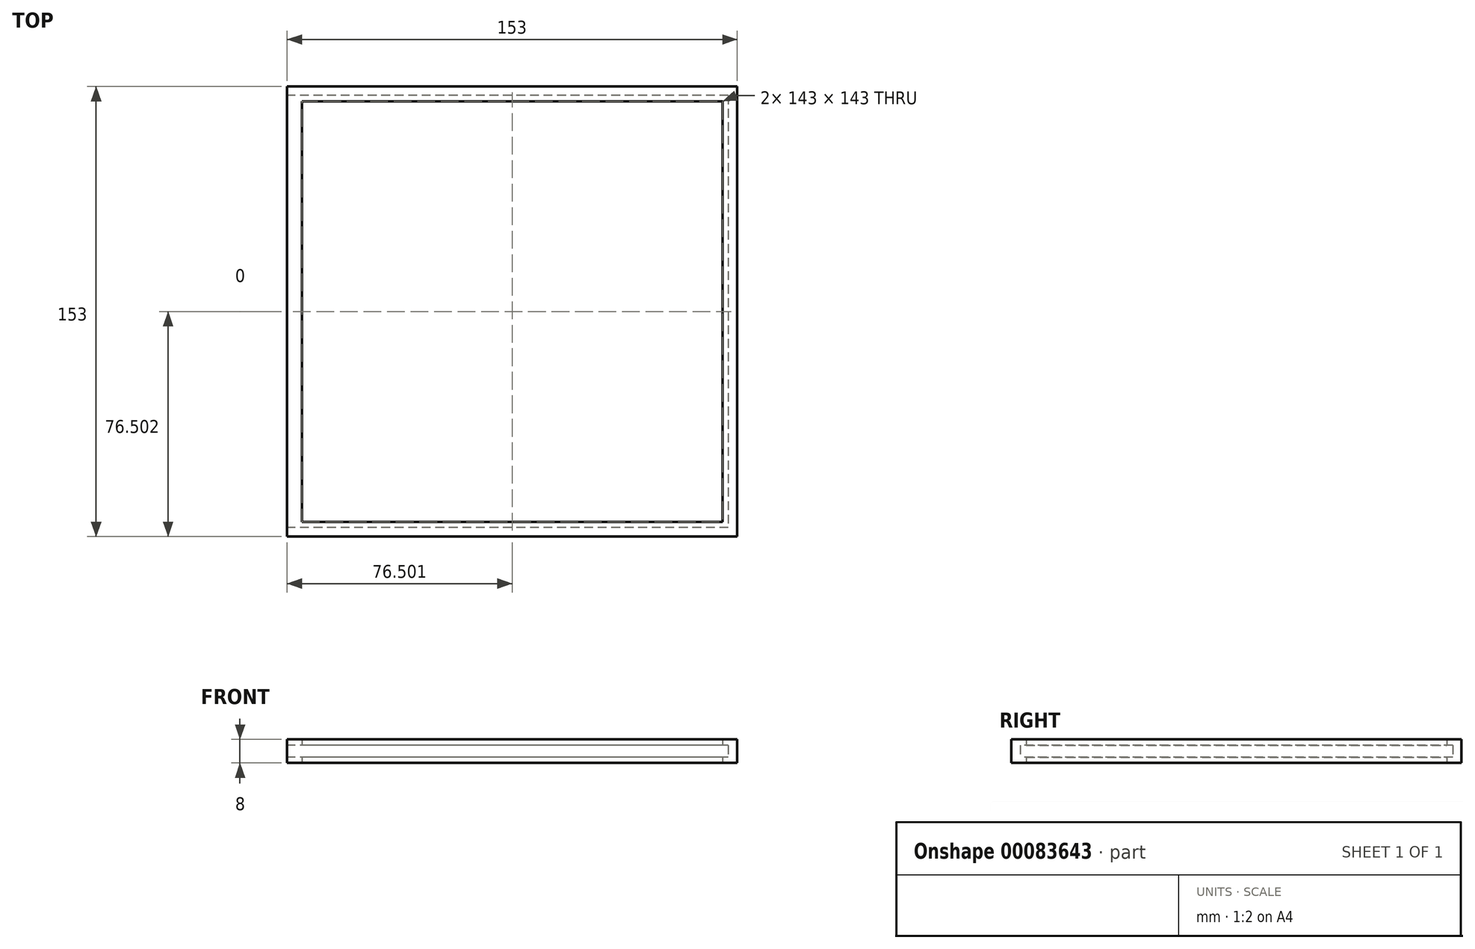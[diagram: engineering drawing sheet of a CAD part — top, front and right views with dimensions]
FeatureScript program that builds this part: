
annotation { "Feature Type Name" : "Feature", "Feature Type Description" : "" }
export const myFeature = defineFeature(function(context is Context, id is Id, definition is map)
    precondition{}
    {
        {
            var Q0;
            Q0=qCreatedBy(makeId("Top.planeOp"),FACE);
            var sketch = newSketch(context, id + "F0", { "sketchPlane" : qUnion([Q0])});
            skLineSegment(sketch, "E0.bottom", {"start": v(-74.33, 69.16) * mm, "end": v(78.67, 69.16) * mm});
            skLineSegment(sketch, "E0.top", {"start": v(-74.33, -83.84) * mm, "end": v(78.67, -83.84) * mm});
            skLineSegment(sketch, "E0.left", {"start": v(-74.33, 69.16) * mm, "end": v(-74.33, -83.84) * mm});
            skLineSegment(sketch, "E0.right", {"start": v(78.67, 69.16) * mm, "end": v(78.67, -83.84) * mm});
            skLineSegment(sketch, "E1.bottom", {"start": v(-69.33, 64.16) * mm, "end": v(73.67, 64.16) * mm});
            skLineSegment(sketch, "E1.top", {"start": v(-69.33, -78.84) * mm, "end": v(73.67, -78.84) * mm});
            skLineSegment(sketch, "E1.left", {"start": v(-69.33, 64.16) * mm, "end": v(-69.33, -78.84) * mm});
            skLineSegment(sketch, "E1.right", {"start": v(73.67, 64.16) * mm, "end": v(73.67, -78.84) * mm});
            skSolve(sketch);
        }
        {
            var Q0;
            Q0=makeQuery(id+"F0.imprint","IMPRINT",FACE,{"disambiguationData":[TD([[makeQuery(id+"F0.imprint","IMPRINT",EDGE,{"derivedFrom":sQuery(id+"F0.wireOp",EDGE,"E0.bottom")}),-1.0]])]});
            extrude(context, id + "F1", {"entities" : qUnion([Q0]), "depth" : 8 * mm});
        }
        {
            var Q0;
            Q0=makeQuery(id+"F1.opExtrude","SWEPT_FACE",FACE,{"disambiguationData":[OSD([sQuery(id+"F0.wireOp",EDGE,"E0.left")])]});
            var sketch = newSketch(context, id + "F2", { "sketchPlane" : qUnion([Q0])});
            skLineSegment(sketch, "E2.bottom", {"start": v(-66.16, 6) * mm, "end": v(80.84, 6) * mm});
            skLineSegment(sketch, "E2.top", {"start": v(-66.16, 2) * mm, "end": v(80.84, 2) * mm});
            skLineSegment(sketch, "E2.left", {"start": v(-66.16, 6) * mm, "end": v(-66.16, 2) * mm});
            skLineSegment(sketch, "E2.right", {"start": v(80.84, 6) * mm, "end": v(80.84, 2) * mm});
            skSolve(sketch);
        }
        {
            var Q0;
            Q0=makeQuery(id+"F2.imprint","IMPRINT",FACE,{"disambiguationData":[TD([[makeQuery(id+"F2.imprint","IMPRINT",EDGE,{"derivedFrom":sQuery(id+"F2.wireOp",EDGE,"E2.bottom")}),-1.0]])]});
            extrude(context, id + "F3", {"entities" : qUnion([Q0]), "operationType" : NewBodyOperationType.REMOVE, "oppositeDirection" : true, "depth" : 150 * mm});
        }
    });
